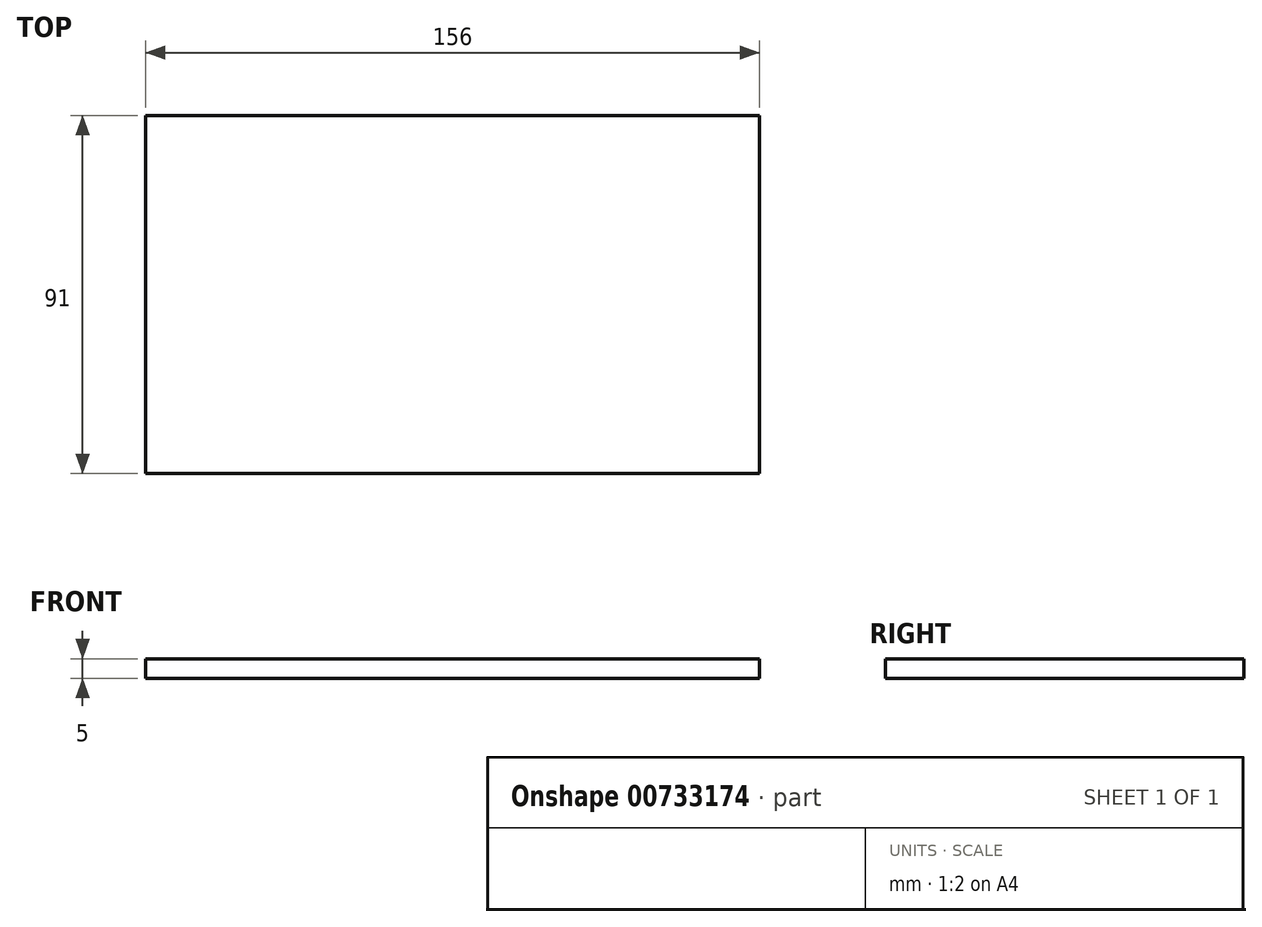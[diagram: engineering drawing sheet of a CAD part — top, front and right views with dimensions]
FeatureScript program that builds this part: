
annotation { "Feature Type Name" : "Feature", "Feature Type Description" : "" }
export const myFeature = defineFeature(function(context is Context, id is Id, definition is map)
    precondition{}
    {
        {
            var Q0;
            Q0=qCreatedBy(makeId("Top.planeOp"),FACE);
            var sketch = newSketch(context, id + "F0", { "sketchPlane" : qUnion([Q0])});
            skLineSegment(sketch, "E0.0", {"start": v(-78, -45.5) * mm, "end": v(-78, 45.5) * mm});
            skLineSegment(sketch, "E0.1", {"start": v(78, 45.5) * mm, "end": v(-78, 45.5) * mm});
            skLineSegment(sketch, "E0.2", {"start": v(78, -45.5) * mm, "end": v(78, 45.5) * mm});
            skLineSegment(sketch, "E0.3", {"start": v(78, -45.5) * mm, "end": v(-78, -45.5) * mm});
            skSolve(sketch);
        }
        {
            var Q0;
            Q0=makeQuery(id+"F0.imprint","IMPRINT",FACE,{"disambiguationData":[TD([[makeQuery(id+"F0.imprint","IMPRINT",EDGE,{"derivedFrom":sQuery(id+"F0.wireOp",EDGE,"E0.0")}),-1.0]])]});
            extrude(context, id + "F1", {"entities" : qUnion([Q0]), "depth" : 5 * mm, "offsetDistance" : 25 * mm});
        }
    });
